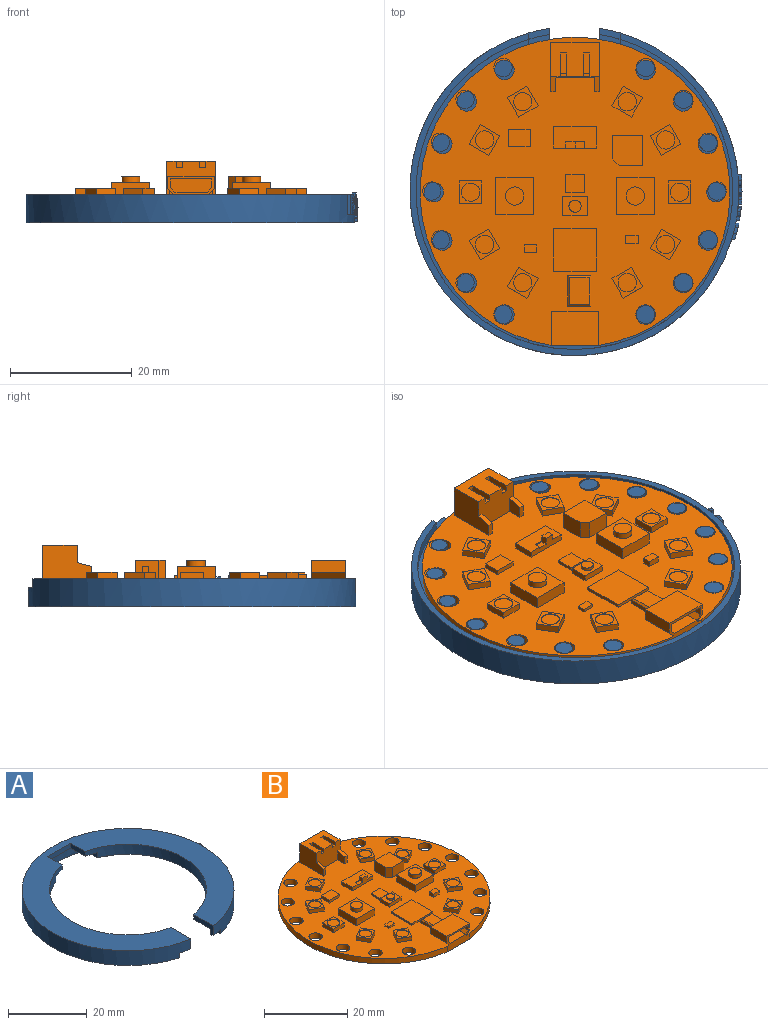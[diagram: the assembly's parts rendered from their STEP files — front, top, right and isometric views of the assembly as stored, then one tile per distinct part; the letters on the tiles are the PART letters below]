
ASSEMBLY  parts=2 mates=1
PART A: 142 faces, bbox 54.5x53.7x4.9 mm
  f0: cylinder r=27mm len=2.67mm, axis (0,0,-1), area 3.2mm2, adj f1,f2,f3,f4,f5,f6,f7,f8
  f1: extruded ~0.6x0.53mm, area 0.3mm2, adj f0,f2,f24,f27
  f2: extruded ~0.51x0.33mm, area 0.2mm2, adj f0,f1,f3,f27
  f3: extruded ~0.52x0.24mm, area 0.2mm2, adj f0,f2,f4,f27
  f4: extruded ~0.54x0.44mm, area 0.2mm2, adj f0,f3,f5,f27
  f5: extruded ~0.53x0.44mm, area 0.2mm2, adj f0,f4,f6,f27
  f6: extruded ~0.51x0.16mm, area 0.1mm2, adj f0,f5,f7,f27
  f7: extruded ~0.52x0.31mm, area 0.2mm2, adj f0,f6,f8,f27
  f8: extruded ~0.52x0.34mm, area 0.2mm2, adj f0,f7,f9,f27
  f9: extruded ~0.53x0.36mm, area 0.2mm2, adj f0,f8,f25,f27
  f10: extruded ~0.9x0.57mm, area 0.5mm2, adj f0,f11,f25,f27
  f11: extruded ~0.75x0.54mm, area 0.4mm2, adj f0,f10,f12,f27
  f12: extruded ~0.53x0.51mm, area 0.3mm2, adj f0,f11,f13,f27
  f13: extruded ~0.5x0.34mm, area 0.2mm2, adj f0,f12,f14,f27
  f14: extruded ~0.51x0.24mm, area 0.2mm2, adj f0,f13,f15,f27
  f15: extruded ~0.52x0.44mm, area 0.2mm2, adj f0,f14,f16,f27
  f16: extruded ~0.52x0.33mm, area 0.2mm2, adj f0,f15,f17,f27
  f17: extruded ~0.51x0.18mm, area 0.1mm2, adj f0,f16,f18,f27
  f18: extruded ~0.5x0.14mm, area 0.1mm2, adj f0,f17,f19,f27
  f19: extruded ~0.53x0.38mm, area 0.2mm2, adj f0,f18,f20,f27
  f20: extruded ~0.52x0.43mm, area 0.2mm2, adj f0,f19,f21,f27
  f21: extruded ~0.52x0.44mm, area 0.2mm2, adj f0,f20,f26,f27
  f22: extruded ~0.51x0.37mm, area 0.2mm2, adj f0,f23,f26,f27
  f23: extruded ~0.52x0.48mm, area 0.2mm2, adj f0,f22,f24,f27
  f24: extruded ~0.82x0.56mm, area 0.4mm2, adj f0,f1,f23,f27
  f25: plane 0.52x0.51mm, normal (0,-0.92,0.39), area 0.3mm2, adj f0,f9,f10,f27
  f26: plane 0.58x0.5mm, normal (0,1,0), area 0.3mm2, adj f0,f21,f22,f27
  f27: cylinder r=27mm len=54mm, axis (0,0,1), area 713.7mm2, adj f1,f2,f3,f4,f5,f6,f7,f8
  f28: cylinder r=27mm len=3.71mm, axis (0,0,-1), area 4.3mm2, adj f29,f30,f31,f32,f33,f34,f35,f36
  f29: plane 2.56x1.02mm, normal (0,0.93,0.37), area 1.4mm2, adj f27,f28,f30,f43
  f30: plane 0.5x0.13mm, normal (0,0.95,-0.31), area 0.1mm2, adj f27,f28,f29,f31
  f31: extruded ~0.51x0.34mm, area 0.2mm2, adj f27,f28,f30,f32
  f32: extruded ~0.52x0.33mm, area 0.2mm2, adj f27,f28,f31,f33
  f33: extruded ~0.52x0.28mm, area 0.1mm2, adj f27,f28,f32,f34
  f34: plane 0.56x0.5mm, normal (0,1,0), area 0.3mm2, adj f27,f28,f33,f35
  f35: extruded ~0.52x0.36mm, area 0.2mm2, adj f27,f28,f34,f36
  f36: extruded ~0.65x0.53mm, area 0.3mm2, adj f27,f28,f35,f37
  f37: extruded ~0.6x0.51mm, area 0.4mm2, adj f27,f28,f36,f38
  f38: plane 2.9x1.09mm, normal (0,-0.94,0.35), area 1.6mm2, adj f27,f28,f37,f39
  f39: plane 0.75x0.51mm, normal (0,0,-1), area 0.4mm2, adj f27,f28,f38,f40
  f40: plane 1.45x0.51mm, normal (0,0.95,-0.31), area 0.8mm2, adj f27,f28,f39,f41
  f41: extruded ~0.5x0.45mm, area 0.2mm2, adj f27,f28,f40,f42
  f42: plane 0.5x0.01mm, normal (0,0,-1), area 0mm2, adj f27,f28,f41,f44
  f43: plane 0.77x0.55mm, normal (0,0,-1), area 0.4mm2, adj f27,f28,f29,f45
  f44: extruded ~0.5x0.45mm, area 0.2mm2, adj f27,f28,f42,f45
  f45: plane 1.45x0.52mm, normal (0,-0.95,-0.32), area 0.8mm2, adj f27,f28,f43,f44
  f46: cylinder r=27mm len=3.58mm, axis (0,0,-1), area 4.8mm2, adj f47,f48,f49,f50,f51,f52,f53,f54
  f47: plane 1.68x0.5mm, normal (0,-1,0), area 0.8mm2, adj f27,f46,f48,f61
  f48: extruded ~0.7x0.52mm, area 0.4mm2, adj f27,f46,f47,f49
  f49: extruded ~0.69x0.58mm, area 0.4mm2, adj f27,f46,f48,f50
  f50: extruded ~0.75x0.61mm, area 0.4mm2, adj f27,f46,f49,f51
  f51: plane 0.51x0.04mm, normal (0,0,-1), area 0mm2, adj f27,f46,f50,f52
  f52: plane 0.5x0.21mm, normal (0,-1,0.08), area 0.1mm2, adj f27,f46,f51,f53
  f53: extruded ~0.5x0.4mm, area 0.2mm2, adj f27,f46,f52,f54
  f54: plane 0.73x0.5mm, normal (0,-1,0), area 0.4mm2, adj f27,f46,f53,f55,f64
  f55: plane 0.7x0.62mm, normal (0,0,-1), area 0.4mm2, adj f46,f54,f56,f64
  f56: plane 3.58x0.5mm, normal (0,1,0), area 1.8mm2, adj f27,f46,f55,f57,f64
  f57: plane 0.7x0.62mm, normal (0,0,1), area 0.4mm2, adj f27,f46,f56,f58
  f58: plane 1.21x0.5mm, normal (0,-1,0), area 0.6mm2, adj f27,f46,f57,f59
  f59: extruded ~0.65x0.52mm, area 0.3mm2, adj f27,f46,f58,f60
  f60: extruded ~0.56x0.43mm, area 0.2mm2, adj f27,f46,f59,f62
  f61: plane 0.7x0.58mm, normal (0,0,1), area 0.4mm2, adj f27,f46,f47,f63
  f62: extruded ~0.56x0.55mm, area 0.4mm2, adj f27,f46,f60,f63
  f63: plane 1.5x0.5mm, normal (0,1,0), area 0.8mm2, adj f27,f46,f61,f62
  f64: cylinder r=27mm len=0.7mm, axis (0,0,-1), area 0.2mm2, adj f54,f55,f56,f113
  f65: cylinder r=27mm len=3.37mm, axis (0,0,-1), area 5.6mm2, adj f66,f67,f68,f69,f70,f71,f72,f73
  f66: plane 0.6x0.38mm, normal (0,0,1), area 0.2mm2, adj f27,f65,f67,f79
  f67: plane 1.29x0.81mm, normal (0,0.85,0.53), area 0.8mm2, adj f27,f65,f66,f68
  f68: plane 0.79x0.67mm, normal (0,0,1), area 0.4mm2, adj f27,f65,f67,f69
  f69: extruded ~1.47x0.99mm, area 0.9mm2, adj f27,f65,f68,f70
  f70: extruded ~0.61x0.46mm, area 0.3mm2, adj f27,f65,f69,f71
  f71: extruded ~0.54x0.53mm, area 0.3mm2, adj f27,f65,f70,f72
  f72: extruded ~0.76x0.57mm, area 0.4mm2, adj f27,f65,f71,f73
  f73: extruded ~1.02x0.75mm, area 0.5mm2, adj f27,f65,f72,f74,f85
  f74: plane 0.98x0.78mm, normal (0,0,-1), area 0.5mm2, adj f65,f73,f80,f85
  f75: plane 0.91x0.5mm, normal (0,-1,0), area 0.5mm2, adj f65,f76,f82,f86
  f76: plane 0.56x0.22mm, normal (0,0,1), area 0.1mm2, adj f65,f75,f77,f86
  f77: extruded ~0.63x0.51mm, area 0.3mm2, adj f65,f76,f78,f86
  f78: extruded ~0.54x0.34mm, area 0.2mm2, adj f65,f77,f83,f86
  f79: plane 1.29x0.5mm, normal (0,-1,0), area 0.6mm2, adj f27,f65,f66,f81
  f80: plane 3.37x0.5mm, normal (0,1,0), area 1.7mm2, adj f27,f65,f74,f81,f85
  f81: plane 0.71x0.71mm, normal (0,0,1), area 0.4mm2, adj f27,f65,f79,f80
  f82: plane 0.56x0.23mm, normal (0,0,-1), area 0.1mm2, adj f65,f75,f84,f86
  f83: extruded ~0.54x0.35mm, area 0.2mm2, adj f65,f78,f84,f86
  f84: extruded ~0.63x0.5mm, area 0.3mm2, adj f65,f82,f83,f86
  f85: cylinder r=27mm len=1.61mm, axis (0,0,-1), area 0.1mm2, adj f73,f74,f80,f113
  f86: cylinder r=27mm len=0.91mm, axis (0,0,1), area 0.7mm2, adj f75,f76,f77,f78,f82,f83,f84
  f87: plane 49.79x20.4mm, normal (0,0,-1), area 292.9mm2, adj f94,f98,f99,f102,f103,f122,f124,f126
  f88: plane 49.79x20.4mm, normal (0,0,-1), area 292.9mm2, adj f93,f97,f99,f107,f108,f114,f116,f118
  f89: plane 3.45x1.8mm, normal (0,0,-1), area 3.5mm2, adj f27,f105,f109,f112
  f90: plane 5.19x1.5mm, normal (1,0,0), area 7.8mm2, adj f91,f94,f95,f96
  f91: plane 8.3x1.5mm, normal (0,-1,0), area 12.5mm2, adj f90,f92,f95,f96
  f92: plane 5.19x1.5mm, normal (-1,0,0), area 7.8mm2, adj f91,f93,f95,f96
  f93: cylinder r=20mm len=39.15mm, axis (0,0,1), area 161mm2, adj f88,f92,f95,f96,f97,f105,f106,f108
  f94: cylinder r=20mm len=39.15mm, axis (0,0,1), area 161mm2, adj f87,f90,f95,f96,f98,f100,f101,f102
  f95: plane 15x7.46mm, normal (0,0,-1), area 51.1mm2, adj f90,f91,f92,f93,f94,f97,f98,f99
  f96: plane 54x53.69mm, normal (0,0,1), area 936mm2, adj f27,f90,f91,f92,f93,f94,f100,f105
  f97: plane 6.35x1.6mm, normal (-1,0,0), area 10.2mm2, adj f88,f93,f95,f99
  f98: plane 6.35x1.6mm, normal (1,0,0), area 10.2mm2, adj f87,f94,f95,f99
  f99: cylinder r=26mm len=52mm, axis (0,0,1), area 246.6mm2, adj f87,f88,f95,f97,f98,f111,f112,f113
  f100: plane 7.11x3.1mm, normal (1,0,0), area 12.3mm2, adj f27,f94,f96,f101,f104,f110
  f101: plane 6.48x3.45mm, normal (0,0,-1), area 20.8mm2, adj f94,f100,f102,f103,f104
  f102: plane 1.9x1.6mm, normal (0,-1,0), area 3mm2, adj f87,f94,f101,f103
  f103: plane 5.69x1.6mm, normal (1,0,0), area 9.1mm2, adj f87,f101,f102,f104
  f104: cylinder r=26mm len=3.45mm, axis (0,0,1), area 5.7mm2, adj f100,f101,f103,f110
  f105: plane 7.11x3.1mm, normal (-1,0,0), area 12.3mm2, adj f27,f89,f93,f96,f106,f109
  f106: plane 6.48x3.45mm, normal (0,0,-1), area 20.8mm2, adj f93,f105,f107,f108,f109
  f107: plane 5.69x1.6mm, normal (-1,0,0), area 9.1mm2, adj f88,f106,f108,f109
  f108: plane 1.9x1.6mm, normal (0,-1,0), area 3mm2, adj f88,f93,f106,f107
  f109: cylinder r=26mm len=3.45mm, axis (0,0,1), area 5.7mm2, adj f89,f105,f106,f107
  f110: plane 3.45x1.8mm, normal (0,0,-1), area 3.5mm2, adj f27,f100,f104,f111
  f111: plane 1.5x1.04mm, normal (1,0,0), area 1.6mm2, adj f27,f99,f110,f113
  f112: plane 1.5x1.04mm, normal (-1,0,0), area 1.6mm2, adj f27,f89,f99,f113
  f113: plane 54x52.94mm, normal (0,0,-1), area 151.3mm2, adj f27,f64,f85,f99,f111,f112
  f114: cylinder r=1.5mm len=3mm, axis (0,0,1), area 14.1mm2, adj f88,f115
  f115: plane 3x3mm, normal (0,0,-1), area 7.1mm2, adj f114
  f116: cylinder r=1.5mm len=3mm, axis (0,0,1), area 14.1mm2, adj f88,f117
  f117: plane 3x3mm, normal (0,0,-1), area 7.1mm2, adj f116
  f118: cylinder r=1.5mm len=3mm, axis (0,0,1), area 14.1mm2, adj f88,f119
  f119: plane 3x3mm, normal (0,0,-1), area 7.1mm2, adj f118
  f120: cylinder r=1.5mm len=3mm, axis (0,0,1), area 14.1mm2, adj f88,f121
  f121: plane 3x3mm, normal (0,0,-1), area 7.1mm2, adj f120
  f122: cylinder r=1.5mm len=3mm, axis (0,0,1), area 14.1mm2, adj f87,f123
  f123: plane 3x3mm, normal (0,0,-1), area 7.1mm2, adj f122
  f124: cylinder r=1.5mm len=3mm, axis (0,0,1), area 14.1mm2, adj f87,f125
  f125: plane 3x3mm, normal (0,0,-1), area 7.1mm2, adj f124
  f126: cylinder r=1.5mm len=3mm, axis (0,0,1), area 14.1mm2, adj f87,f127
  f127: plane 3x3mm, normal (0,0,-1), area 7.1mm2, adj f126
  f128: cylinder r=1.5mm len=3mm, axis (0,0,1), area 14.1mm2, adj f87,f129
  f129: plane 3x3mm, normal (0,0,-1), area 7.1mm2, adj f128
  f130: cylinder r=1.5mm len=3mm, axis (0,0,1), area 14.1mm2, adj f87,f131
  f131: plane 3x3mm, normal (0,0,-1), area 7.1mm2, adj f130
  f132: cylinder r=1.5mm len=3mm, axis (0,0,1), area 14.1mm2, adj f87,f133
  f133: plane 3x3mm, normal (0,0,-1), area 7.1mm2, adj f132
  f134: cylinder r=1.5mm len=3mm, axis (0,0,1), area 14.1mm2, adj f87,f135
  f135: plane 3x3mm, normal (0,0,-1), area 7.1mm2, adj f134
  f136: cylinder r=1.5mm len=3mm, axis (0,0,1), area 14.1mm2, adj f88,f137
  f137: plane 3x3mm, normal (0,0,-1), area 7.1mm2, adj f136
  f138: cylinder r=1.5mm len=3mm, axis (0,0,1), area 14.1mm2, adj f88,f139
  f139: plane 3x3mm, normal (0,0,-1), area 7.1mm2, adj f138
  f140: cylinder r=1.5mm len=3mm, axis (0,0,1), area 14.1mm2, adj f88,f141
  f141: plane 3x3mm, normal (0,0,-1), area 7.1mm2, adj f140
PART B: 202 faces, bbox 50.9x50.6x7.1 mm
  f0: plane 50.86x50.58mm, normal (0,0,1), area 1470.2mm2, adj f1,f2,f3,f4,f5,f6,f7,f8
  f1: cylinder r=1.6mm len=3.2mm, axis (0,0,-1), area 16.1mm2, adj f0,f17
  f2: cylinder r=1.6mm len=3.2mm, axis (0,0,-1), area 16.1mm2, adj f0,f17
  f3: cylinder r=1.6mm len=3.2mm, axis (0,0,-1), area 16.1mm2, adj f0,f17
  f4: cylinder r=1.6mm len=3.2mm, axis (0,0,-1), area 16.1mm2, adj f0,f17
  f5: cylinder r=1.6mm len=3.2mm, axis (0,0,-1), area 16.1mm2, adj f0,f17
  f6: cylinder r=1.6mm len=3.2mm, axis (0,0,-1), area 16.1mm2, adj f0,f17
  f7: cylinder r=1.6mm len=3.2mm, axis (0,0,-1), area 16.1mm2, adj f0,f17
  f8: cylinder r=1.6mm len=3.2mm, axis (0,0,-1), area 16.1mm2, adj f0,f17
  f9: cylinder r=1.6mm len=3.2mm, axis (0,0,-1), area 16.1mm2, adj f0,f17
  f10: cylinder r=1.6mm len=3.2mm, axis (0,0,-1), area 16.1mm2, adj f0,f17
  f11: cylinder r=1.6mm len=3.2mm, axis (0,0,-1), area 16.1mm2, adj f0,f17
  f12: cylinder r=1.6mm len=3.2mm, axis (0,0,-1), area 16.1mm2, adj f0,f17
  f13: cylinder r=1.6mm len=3.2mm, axis (0,0,-1), area 16.1mm2, adj f0,f17
  f14: cylinder r=1.6mm len=3.2mm, axis (0,0,-1), area 16.1mm2, adj f0,f17
  f15: plane 7.6x4.6mm, normal (0,-1,0), area 19.5mm2, adj f0,f16,f17,f18,f19,f21,f22,f23
  f16: cylinder r=25.43mm len=50.86mm, axis (0,0,-1), area 243.6mm2, adj f0,f15,f17
  f17: plane 50.86x50.58mm, normal (0,0,-1), area 1917.6mm2, adj f1,f2,f3,f4,f5,f6,f7,f8
  f18: plane 5.2x0.77mm, normal (-0.71,0,0.71), area 5.6mm2, adj f15,f19,f20,f24
  f19: plane 5.2x1.43mm, normal (-1,0,0), area 7.5mm2, adj f15,f18,f20,f23
  f20: plane 6.8x2.2mm, normal (0,-1,0), area 14.4mm2, adj f18,f19,f21,f22,f23,f24
  f21: plane 5.2x0.77mm, normal (0.71,0,0.71), area 5.6mm2, adj f15,f20,f22,f24
  f22: plane 5.2x1.43mm, normal (1,0,0), area 7.5mm2, adj f15,f20,f21,f23
  f23: plane 6.8x5.2mm, normal (0,0,-1), area 35.4mm2, adj f15,f19,f20,f22
  f24: plane 5.27x5.2mm, normal (0,0,1), area 27.4mm2, adj f15,f18,f20,f21
  f25: plane 5.6x1mm, normal (0.71,0,-0.71), area 7.9mm2, adj f0,f15,f26,f27
  f26: plane 5.6x2mm, normal (1,0,0), area 11.2mm2, adj f15,f25,f27,f30
  f27: plane 7.6x3mm, normal (0,1,0), area 21.8mm2, adj f0,f25,f26,f28,f29,f30
  f28: plane 5.6x1mm, normal (-0.71,0,-0.71), area 7.9mm2, adj f0,f15,f27,f29
  f29: plane 5.6x2mm, normal (-1,0,0), area 11.2mm2, adj f15,f27,f28,f30
  f30: plane 7.6x5.6mm, normal (0,0,1), area 42.6mm2, adj f15,f26,f27,f29
  f31: plane 5x2.5mm, normal (0,0,-1), area 9.2mm2, adj f33,f38,f39,f40,f42,f43,f55
  f32: plane 5x2.5mm, normal (0,0,-1), area 9.2mm2, adj f35,f36,f39,f44,f46,f47,f55
  f33: plane 5x0.5mm, normal (1,0,0), area 2.5mm2, adj f31,f34,f39,f55
  f34: plane 5x1mm, normal (0,0,-1), area 5mm2, adj f33,f35,f39,f55
  f35: plane 5x0.5mm, normal (-1,0,0), area 2.5mm2, adj f32,f34,f39,f55
  f36: plane 5x3.5mm, normal (-1,0,0), area 17.5mm2, adj f32,f37,f39,f55
  f37: plane 6x5mm, normal (0,0,1), area 30mm2, adj f36,f38,f39,f55
  f38: plane 5x3.5mm, normal (1,0,0), area 17.5mm2, adj f31,f37,f39,f55
  f39: plane 6x4mm, normal (0,1,0), area 21.5mm2, adj f31,f32,f33,f34,f35,f36,f37,f38
  f40: plane 3.93x1mm, normal (-1,0,0), area 3.9mm2, adj f31,f41,f42,f48,f58
  f41: plane 1x0.6mm, normal (0,0,1), area 0.6mm2, adj f39,f40,f43,f48
  f42: plane 1x1mm, normal (0,-1,0), area 1mm2, adj f31,f40,f43,f58
  f43: plane 3.93x1mm, normal (1,0,0), area 3.9mm2, adj f31,f41,f42,f48,f58
  f44: plane 3.93x1mm, normal (-1,0,0), area 3.9mm2, adj f32,f45,f46,f48,f58
  f45: plane 1x0.6mm, normal (0,0,1), area 0.6mm2, adj f39,f44,f47,f48
  f46: plane 1x1mm, normal (0,-1,0), area 1mm2, adj f32,f44,f47,f58
  f47: plane 3.93x1mm, normal (1,0,0), area 3.9mm2, adj f32,f45,f46,f48,f58
  f48: plane 8x5.5mm, normal (0,-1,0), area 37.8mm2, adj f0,f40,f41,f43,f44,f45,f47,f49
  f49: plane 2.64x2.4mm, normal (-1,0,0), area 5.6mm2, adj f0,f48,f50,f51
  f50: plane 2x0.8mm, normal (0,-1,0), area 1.6mm2, adj f0,f49,f51,f56
  f51: plane 2.4x0.8mm, normal (0,-0.26,0.97), area 2mm2, adj f48,f49,f50,f56
  f52: plane 2.64x2.4mm, normal (1,0,0), area 5.6mm2, adj f0,f48,f53,f54
  f53: plane 2x0.8mm, normal (0,-1,0), area 1.6mm2, adj f0,f52,f54,f57
  f54: plane 2.4x0.8mm, normal (0,-0.26,0.97), area 2mm2, adj f48,f52,f53,f57
  f55: plane 8x5.5mm, normal (0,1,0), area 22.5mm2, adj f0,f31,f32,f33,f34,f35,f36,f37
  f56: plane 8x5.5mm, normal (1,0,0), area 36.4mm2, adj f0,f48,f50,f51,f55,f58
  f57: plane 8x5.5mm, normal (-1,0,0), area 36.4mm2, adj f0,f48,f53,f54,f55,f58
  f58: plane 8x5.6mm, normal (0,0,1), area 36.9mm2, adj f40,f42,f43,f44,f46,f47,f48,f55
  f59: cylinder r=1.5mm len=3mm, axis (0,0,1), area 9.4mm2, adj f60,f65
  f60: plane 3x3mm, normal (0,0,1), area 7.1mm2, adj f59
  f61: plane 6.2x2mm, normal (1,0,0), area 12.4mm2, adj f0,f62,f64,f65
  f62: plane 6.2x2mm, normal (0,-1,0), area 12.4mm2, adj f0,f61,f63,f65
  f63: plane 6.2x2mm, normal (-1,0,0), area 12.4mm2, adj f0,f62,f64,f65
  f64: plane 6.2x2mm, normal (0,1,0), area 12.4mm2, adj f0,f61,f63,f65
  f65: plane 6.2x6.2mm, normal (0,0,1), area 31.4mm2, adj f59,f61,f62,f63,f64
  f66: cylinder r=1.5mm len=3mm, axis (0,0,-1), area 9.4mm2, adj f67,f72
  f67: plane 3x3mm, normal (0,0,1), area 7.1mm2, adj f66
  f68: plane 6.2x2mm, normal (-1,0,0), area 12.4mm2, adj f0,f69,f71,f72
  f69: plane 6.2x2mm, normal (0,-1,0), area 12.4mm2, adj f0,f68,f70,f72
  f70: plane 6.2x2mm, normal (1,0,0), area 12.4mm2, adj f0,f69,f71,f72
  f71: plane 6.2x2mm, normal (0,1,0), area 12.4mm2, adj f0,f68,f70,f72
  f72: plane 6.2x6.2mm, normal (0,0,1), area 31.4mm2, adj f66,f68,f69,f70,f71
  f73: plane 3x3mm, normal (0,0,1), area 7.1mm2, adj f74
  f74: cylinder r=1.5mm len=3mm, axis (0,0,1), area 0.9mm2, adj f73,f79
  f75: plane 3.2x1.85mm, normal (-0.5,-0.87,0), area 4.1mm2, adj f0,f76,f78,f79
  f76: plane 3.2x1.85mm, normal (-0.87,0.5,0), area 4.1mm2, adj f0,f75,f77,f79
  f77: plane 3.2x1.85mm, normal (0.5,0.87,0), area 4.1mm2, adj f0,f76,f78,f79
  f78: plane 3.2x1.85mm, normal (0.87,-0.5,0), area 4.1mm2, adj f0,f75,f77,f79
  f79: plane 5.05x5.05mm, normal (0,0,1), area 6.6mm2, adj f74,f75,f76,f77,f78
  f80: plane 3x3mm, normal (0,0,1), area 7.1mm2, adj f81
  f81: cylinder r=1.5mm len=3mm, axis (0,0,1), area 0.9mm2, adj f80,f86
  f82: plane 3.2x1.85mm, normal (-0.5,0.87,0), area 4.1mm2, adj f0,f83,f85,f86
  f83: plane 3.2x1.85mm, normal (0.87,0.5,0), area 4.1mm2, adj f0,f82,f84,f86
  f84: plane 3.2x1.85mm, normal (0.5,-0.87,0), area 4.1mm2, adj f0,f83,f85,f86
  f85: plane 3.2x1.85mm, normal (-0.87,-0.5,0), area 4.1mm2, adj f0,f82,f84,f86
  f86: plane 5.05x5.05mm, normal (0,0,1), area 6.6mm2, adj f81,f82,f83,f84,f85
  f87: plane 3x3mm, normal (0,0,1), area 7.1mm2, adj f88
  f88: cylinder r=1.5mm len=3mm, axis (0,0,1), area 0.9mm2, adj f87,f93
  f89: plane 3.7x1.1mm, normal (1,0,0), area 4.1mm2, adj f0,f90,f92,f93
  f90: plane 3.7x1.1mm, normal (0,-1,0), area 4.1mm2, adj f0,f89,f91,f93
  f91: plane 3.7x1.1mm, normal (-1,0,0), area 4.1mm2, adj f0,f90,f92,f93
  f92: plane 3.7x1.1mm, normal (0,1,0), area 4.1mm2, adj f0,f89,f91,f93
  f93: plane 3.7x3.7mm, normal (0,0,1), area 6.6mm2, adj f88,f89,f90,f91,f92
  f94: plane 3x3mm, normal (0,0,1), area 7.1mm2, adj f95
  f95: cylinder r=1.5mm len=3mm, axis (0,0,1), area 0.9mm2, adj f94,f100
  f96: plane 3.2x1.85mm, normal (-0.87,0.5,0), area 4.1mm2, adj f0,f97,f99,f100
  f97: plane 3.2x1.85mm, normal (0.5,0.87,0), area 4.1mm2, adj f0,f96,f98,f100
  f98: plane 3.2x1.85mm, normal (0.87,-0.5,0), area 4.1mm2, adj f0,f97,f99,f100
  f99: plane 3.2x1.85mm, normal (-0.5,-0.87,0), area 4.1mm2, adj f0,f96,f98,f100
  f100: plane 5.05x5.05mm, normal (0,0,1), area 6.6mm2, adj f95,f96,f97,f98,f99
  f101: plane 3x3mm, normal (0,0,1), area 7.1mm2, adj f102
  f102: cylinder r=1.5mm len=3mm, axis (0,0,1), area 0.9mm2, adj f101,f107
  f103: plane 3.2x1.85mm, normal (0.5,-0.87,0), area 4.1mm2, adj f0,f104,f106,f107
  f104: plane 3.2x1.85mm, normal (-0.87,-0.5,0), area 4.1mm2, adj f0,f103,f105,f107
  f105: plane 3.2x1.85mm, normal (-0.5,0.87,0), area 4.1mm2, adj f0,f104,f106,f107
  f106: plane 3.2x1.85mm, normal (0.87,0.5,0), area 4.1mm2, adj f0,f103,f105,f107
  f107: plane 5.05x5.05mm, normal (0,0,1), area 6.6mm2, adj f102,f103,f104,f105,f106
  f108: plane 3x3mm, normal (0,0,1), area 7.1mm2, adj f109
  f109: cylinder r=1.5mm len=3mm, axis (0,0,1), area 0.9mm2, adj f108,f114
  f110: plane 3.2x1.85mm, normal (-0.87,-0.5,0), area 4.1mm2, adj f0,f111,f113,f114
  f111: plane 3.2x1.85mm, normal (-0.5,0.87,0), area 4.1mm2, adj f0,f110,f112,f114
  f112: plane 3.2x1.85mm, normal (0.87,0.5,0), area 4.1mm2, adj f0,f111,f113,f114
  f113: plane 3.2x1.85mm, normal (0.5,-0.87,0), area 4.1mm2, adj f0,f110,f112,f114
  f114: plane 5.05x5.05mm, normal (0,0,1), area 6.6mm2, adj f109,f110,f111,f112,f113
  f115: plane 3x3mm, normal (0,0,1), area 7.1mm2, adj f116
  f116: cylinder r=1.5mm len=3mm, axis (0,0,1), area 0.9mm2, adj f115,f121
  f117: plane 3.2x1.85mm, normal (0.5,0.87,0), area 4.1mm2, adj f0,f118,f120,f121
  f118: plane 3.2x1.85mm, normal (0.87,-0.5,0), area 4.1mm2, adj f0,f117,f119,f121
  f119: plane 3.2x1.85mm, normal (-0.5,-0.87,0), area 4.1mm2, adj f0,f118,f120,f121
  f120: plane 3.2x1.85mm, normal (-0.87,0.5,0), area 4.1mm2, adj f0,f117,f119,f121
  f121: plane 5.05x5.05mm, normal (0,0,1), area 6.6mm2, adj f116,f117,f118,f119,f120
  f122: plane 3x3mm, normal (0,0,1), area 7.1mm2, adj f123
  f123: cylinder r=1.5mm len=3mm, axis (0,0,1), area 0.9mm2, adj f122,f128
  f124: plane 3.2x1.85mm, normal (0.87,0.5,0), area 4.1mm2, adj f0,f125,f127,f128
  f125: plane 3.2x1.85mm, normal (0.5,-0.87,0), area 4.1mm2, adj f0,f124,f126,f128
  f126: plane 3.2x1.85mm, normal (-0.87,-0.5,0), area 4.1mm2, adj f0,f125,f127,f128
  f127: plane 3.2x1.85mm, normal (-0.5,0.87,0), area 4.1mm2, adj f0,f124,f126,f128
  f128: plane 5.05x5.05mm, normal (0,0,1), area 6.6mm2, adj f123,f124,f125,f126,f127
  f129: plane 3x3mm, normal (0,0,1), area 7.1mm2, adj f130
  f130: cylinder r=1.5mm len=3mm, axis (0,0,1), area 0.9mm2, adj f129,f135
  f131: plane 3.7x1.1mm, normal (-1,0,0), area 4.1mm2, adj f0,f132,f134,f135
  f132: plane 3.7x1.1mm, normal (0,1,0), area 4.1mm2, adj f0,f131,f133,f135
  f133: plane 3.7x1.1mm, normal (1,0,0), area 4.1mm2, adj f0,f132,f134,f135
  f134: plane 3.7x1.1mm, normal (0,-1,0), area 4.1mm2, adj f0,f131,f133,f135
  f135: plane 3.7x3.7mm, normal (0,0,1), area 6.6mm2, adj f130,f131,f132,f133,f134
  f136: plane 3x3mm, normal (0,0,1), area 7.1mm2, adj f137
  f137: cylinder r=1.5mm len=3mm, axis (0,0,1), area 0.9mm2, adj f136,f142
  f138: plane 3.2x1.85mm, normal (0.87,-0.5,0), area 4.1mm2, adj f0,f139,f141,f142
  f139: plane 3.2x1.85mm, normal (-0.5,-0.87,0), area 4.1mm2, adj f0,f138,f140,f142
  f140: plane 3.2x1.85mm, normal (-0.87,0.5,0), area 4.1mm2, adj f0,f139,f141,f142
  f141: plane 3.2x1.85mm, normal (0.5,0.87,0), area 4.1mm2, adj f0,f138,f140,f142
  f142: plane 5.05x5.05mm, normal (0,0,1), area 6.6mm2, adj f137,f138,f139,f140,f141
  f143: plane 1x1mm, normal (1,0,0), area 1mm2, adj f144,f146,f150,f154
  f144: plane 1.5x1mm, normal (0,1,0), area 1.5mm2, adj f143,f145,f146,f150
  f145: plane 1.2x1mm, normal (-1,0,0), area 1.2mm2, adj f144,f146,f147,f149,f154
  f146: plane 1.5x1mm, normal (0,0,1), area 1.5mm2, adj f143,f144,f145,f154
  f147: plane 1.5x1mm, normal (0,0,1), area 1.5mm2, adj f145,f148,f149,f154
  f148: plane 1x0.2mm, normal (1,0,0), area 0.2mm2, adj f147,f149,f150,f154
  f149: plane 1.5x0.2mm, normal (0,-1,0), area 0.3mm2, adj f145,f147,f148,f150
  f150: plane 7x3.55mm, normal (0,0,1), area 21.9mm2, adj f143,f144,f148,f149,f151,f152,f153,f154
  f151: plane 3.55x1mm, normal (-1,0,0), area 3.5mm2, adj f0,f150,f152,f154
  f152: plane 7x1mm, normal (0,1,0), area 7mm2, adj f0,f150,f151,f153
  f153: plane 3.55x1mm, normal (1,0,0), area 3.5mm2, adj f0,f150,f152,f154
  f154: plane 7x2mm, normal (0,-1,0), area 8.2mm2, adj f0,f143,f145,f146,f147,f148,f150,f151
  f155: plane 3x1.1mm, normal (-0.71,-0.71,0), area 4.7mm2, adj f0,f156,f157,f158
  f156: plane 5x5mm, normal (0,0,1), area 24.4mm2, adj f155,f157,f158,f159,f160
  f157: plane 3.9x3mm, normal (0,-1,0), area 11.7mm2, adj f0,f155,f156,f160
  f158: plane 3.9x3mm, normal (-1,0,0), area 11.7mm2, adj f0,f155,f156,f159
  f159: plane 5x3mm, normal (0,1,0), area 15mm2, adj f0,f156,f158,f160
  f160: plane 5x3mm, normal (1,0,0), area 15mm2, adj f0,f156,f157,f159
  f161: plane 2.8x0.8mm, normal (1,0,0), area 2.2mm2, adj f0,f162,f164,f165
  f162: plane 3.56x0.8mm, normal (0,-1,0), area 2.8mm2, adj f0,f161,f163,f165
  f163: plane 2.8x0.8mm, normal (-1,0,0), area 2.2mm2, adj f0,f162,f164,f165
  f164: plane 3.56x0.8mm, normal (0,1,0), area 2.8mm2, adj f0,f161,f163,f165
  f165: plane 3.56x2.8mm, normal (0,0,1), area 10mm2, adj f161,f162,f163,f164
  f166: cylinder r=1mm len=2mm, axis (0,0,1), area 3.1mm2, adj f167,f172
  f167: plane 2x2mm, normal (0,0,1), area 3.1mm2, adj f166
  f168: plane 3x1mm, normal (1,0,0), area 3mm2, adj f0,f169,f171,f172
  f169: plane 4x1mm, normal (0,-1,0), area 4mm2, adj f0,f168,f170,f172
  f170: plane 3x1mm, normal (-1,0,0), area 3mm2, adj f0,f169,f171,f172
  f171: plane 4x1mm, normal (0,1,0), area 4mm2, adj f0,f168,f170,f172
  f172: plane 4x3mm, normal (0,0,1), area 8.9mm2, adj f166,f168,f169,f170,f171
  f173: plane 1.4x1mm, normal (1,0,0), area 1.4mm2, adj f0,f174,f176,f177
  f174: plane 2x1mm, normal (0,-1,0), area 2mm2, adj f0,f173,f175,f177
  f175: plane 1.4x1mm, normal (-1,0,0), area 1.4mm2, adj f0,f174,f176,f177
  f176: plane 2x1mm, normal (0,1,0), area 2mm2, adj f0,f173,f175,f177
  f177: plane 2x1.4mm, normal (0,0,1), area 2.8mm2, adj f173,f174,f175,f176
  f178: plane 7x0.5mm, normal (-1,0,0), area 3.5mm2, adj f0,f179,f181,f182
  f179: plane 7x0.5mm, normal (0,1,0), area 3.5mm2, adj f0,f178,f180,f182
  f180: plane 7x0.5mm, normal (1,0,0), area 3.5mm2, adj f0,f179,f181,f182
  f181: plane 7x0.5mm, normal (0,-1,0), area 3.5mm2, adj f0,f178,f180,f182
  f182: plane 7x7mm, normal (0,0,1), area 49mm2, adj f178,f179,f180,f181
  f183: plane 5x0.3mm, normal (-0.71,0,0.71), area 2mm2, adj f184,f186,f188,f189
  f184: plane 3.8x0.3mm, normal (0,0.71,0.71), area 1.5mm2, adj f183,f185,f189,f190
  f185: plane 5x0.3mm, normal (0.71,0,0.71), area 2mm2, adj f184,f186,f189,f191
  f186: plane 3.8x0.3mm, normal (0,-0.71,0.71), area 1.5mm2, adj f183,f185,f187,f189
  f187: plane 3.8x0.7mm, normal (0,-1,0), area 2.7mm2, adj f0,f186,f188,f191
  f188: plane 5x0.7mm, normal (-1,0,0), area 3.5mm2, adj f0,f183,f187,f190
  f189: plane 4.4x3.2mm, normal (0,0,1), area 14.1mm2, adj f183,f184,f185,f186
  f190: plane 3.8x0.7mm, normal (0,1,0), area 2.7mm2, adj f0,f184,f188,f191
  f191: plane 5x0.7mm, normal (1,0,0), area 3.5mm2, adj f0,f185,f187,f190
  f192: plane 3x0.5mm, normal (-1,0,0), area 1.5mm2, adj f0,f193,f195,f196
  f193: plane 3x0.5mm, normal (0,1,0), area 1.5mm2, adj f0,f192,f194,f196
  f194: plane 3x0.5mm, normal (1,0,0), area 1.5mm2, adj f0,f193,f195,f196
  f195: plane 3x0.5mm, normal (0,-1,0), area 1.5mm2, adj f0,f192,f194,f196
  f196: plane 3x3mm, normal (0,0,1), area 9mm2, adj f192,f193,f194,f195
  f197: plane 1.3x0.5mm, normal (-1,0,0), area 0.6mm2, adj f0,f198,f200,f201
  f198: plane 2x0.5mm, normal (0,1,0), area 1mm2, adj f0,f197,f199,f201
  f199: plane 1.3x0.5mm, normal (1,0,0), area 0.6mm2, adj f0,f198,f200,f201
  f200: plane 2x0.5mm, normal (0,-1,0), area 1mm2, adj f0,f197,f199,f201
  f201: plane 2x1.3mm, normal (0,0,1), area 2.6mm2, adj f197,f198,f199,f200
PLACE A rot(axis=(-1,0,0),180deg) t=(3.14,-5.16,1.84)mm fixed
PLACE B rot(axis=(1,0,0),0deg) t=(3.25,-5.36,6.44)mm
MATE slider B.f1 <-> A.f120  axis (0,0,1) through (14.84,-25.43,6.44)mm
